# Revit family: Zumtobel Track U SUP2
name_source: partatom
category: Lighting Fixtures
revit_build: Autodesk Revit 2016 (Build: 20150220_1215(x64)
units: mm (PartAtom-declared; Revit-internal decimal feet)

## family parameters
Cut with Voids When Loaded = No
Host = Face
Light Source = No
OmniClass Number = 23.80.70.11
OmniClass Title = Luminaries for Internal Lighting
Part Type = Normal
Room Calculation Point = No
Round Connector Dimension = Use Diameter
Shared = No

## types (3) — shared parameters
Apparent Load = 0 VA
Assembly Code = D5020200
Description = Track SUP2
Emit Shape Visible in Rendering = No
Manufacturer = Zumtobel Lighting
URL = http://www.zumtobel.com
zero-valued in all types: Default Elevation

## per-type parameters (varying)
| type | Length | Model |
| SUP2 TRACK U 4M | 4000 mm  [stored 13.1234 ft] | 22169723 |
| SUP2 TRACK U 2M | 2000 mm | 22169729 |
| SUP2 TRACK U 3M | 4000 mm  [stored 13.1234 ft] | 22169723 |

note: [stored X ft] marks values corroborated as IEEE doubles in the binary element streams (Revit-internal decimal feet)

## geometry (parser evidence)
native form markers: Sweep x5
no freeform markers — native parametric forms only
